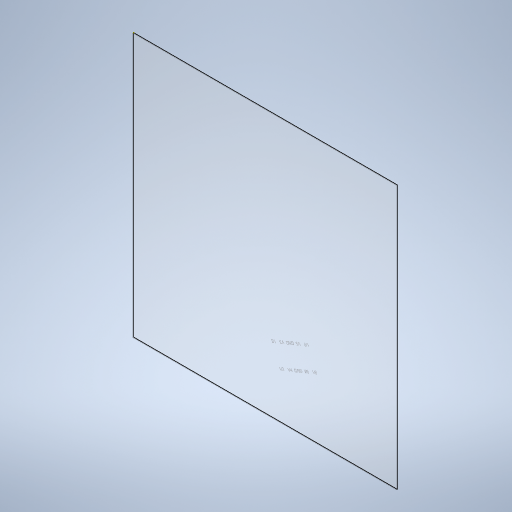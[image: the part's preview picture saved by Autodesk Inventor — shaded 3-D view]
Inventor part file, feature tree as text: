
AUTODESK INVENTOR PART (.ipt)
format: ipt  version: 2024.2 (Build 282272000, 272)  size: 284,160 bytes
history: native  units: in
note: dims shown in document units (in); Inventor stores cm internally (conversion verified against a paired STEP export)
features: sketch x1, extrude x1, other x1
ambient origin geometry x8: Origin, YZ Plane, XZ Plane, XY Plane, X Axis, Y Axis, Z Axis, Center Point
bodies: Solid1 (feature_tree)
feature tree (3):
  sketch  "Sketch1"  dims[d5=2.96in d9=0.01in d10=0.0in]
  extrude  "Extrusion1"  Depth=0.01in TaperAngle=0.0deg
  other  "Image1"
